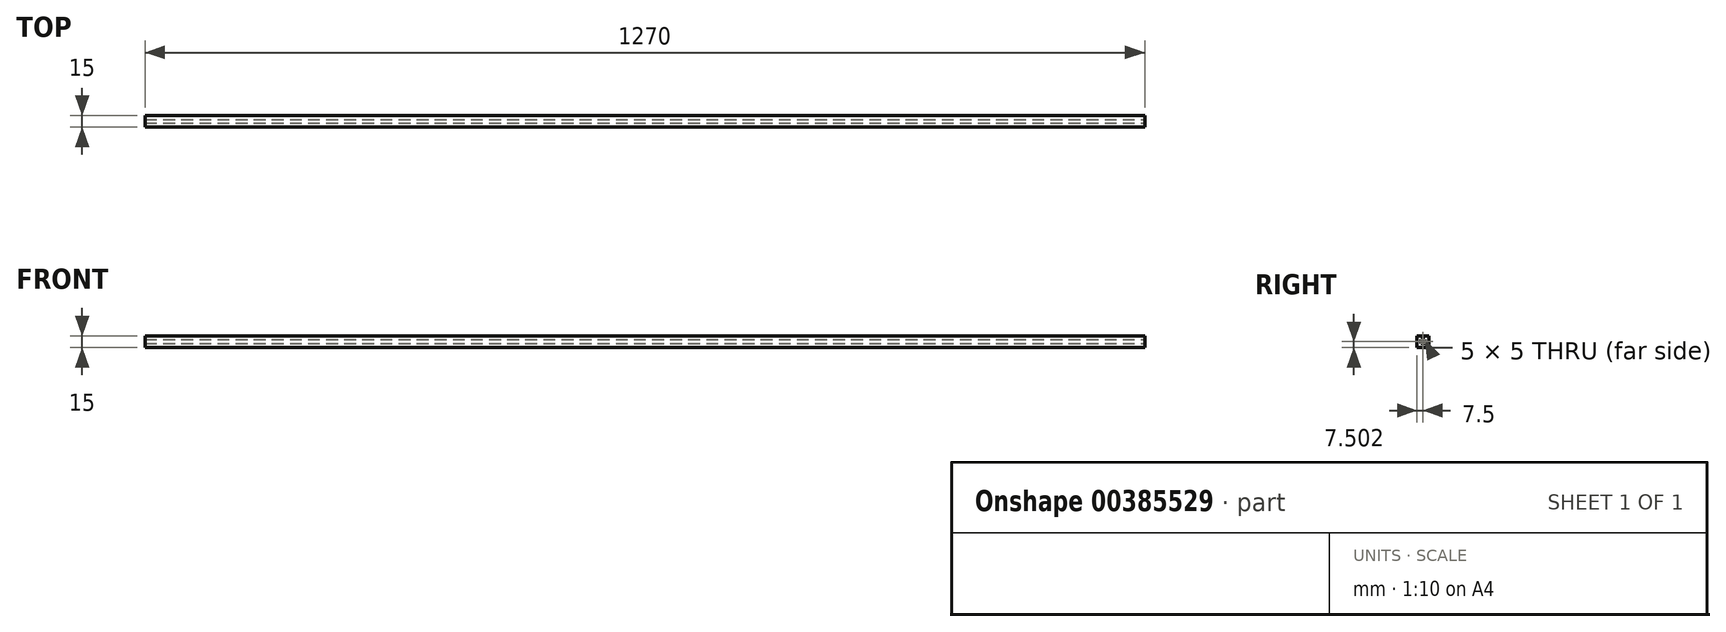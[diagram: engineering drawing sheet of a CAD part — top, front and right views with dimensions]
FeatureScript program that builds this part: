
annotation { "Feature Type Name" : "Feature", "Feature Type Description" : "" }
export const myFeature = defineFeature(function(context is Context, id is Id, definition is map)
    precondition{}
    {
        {
            var Q0;
            Q0=qCreatedBy(makeId("Front.planeOp"),FACE);
            var sketch = newSketch(context, id + "F0", { "sketchPlane" : qUnion([Q0])});
            skLineSegment(sketch, "E0.bottom", {"start": v(-638.32, -20.5) * mm, "end": v(631.68, -20.5) * mm});
            skLineSegment(sketch, "E0.top", {"start": v(-638.32, -35.5) * mm, "end": v(631.68, -35.5) * mm});
            skLineSegment(sketch, "E0.left", {"start": v(-638.32, -20.5) * mm, "end": v(-638.32, -35.5) * mm});
            skLineSegment(sketch, "E0.right", {"start": v(631.68, -20.5) * mm, "end": v(631.68, -35.5) * mm});
            skSolve(sketch);
        }
        {
            var Q0;
            Q0=makeQuery(id+"F0.imprint","IMPRINT",FACE,{"disambiguationData":[TD([[makeQuery(id+"F0.imprint","IMPRINT",EDGE,{"derivedFrom":sQuery(id+"F0.wireOp",EDGE,"E0.bottom")}),-1.0]])]});
            extrude(context, id + "F1", {"entities" : qUnion([Q0]), "endBound" : BoundingType.SYMMETRIC, "depth" : 15 * mm});
        }
        {
            var Q0;
            Q0=makeQuery(id+"F1.opExtrude","SWEPT_FACE",FACE,{"disambiguationData":[OSD([sQuery(id+"F0.wireOp",EDGE,"E0.right")])]});
            var sketch = newSketch(context, id + "F2", { "sketchPlane" : qUnion([Q0])});
            skLineSegment(sketch, "E1.0", {"start": v(2.5, -30.5) * mm, "end": v(2.5, -25.5) * mm});
            skLineSegment(sketch, "E1.1", {"start": v(-2.5, -30.5) * mm, "end": v(2.5, -30.5) * mm});
            skLineSegment(sketch, "E1.2", {"start": v(-2.5, -25.5) * mm, "end": v(-2.5, -30.5) * mm});
            skLineSegment(sketch, "E1.3", {"start": v(2.5, -25.5) * mm, "end": v(-2.5, -25.5) * mm});
            skSolve(sketch);
        }
        {
            var Q0;
            Q0=makeQuery(id+"F2.imprint","IMPRINT",FACE,{"disambiguationData":[TD([[makeQuery(id+"F2.imprint","IMPRINT",EDGE,{"derivedFrom":sQuery(id+"F2.wireOp",EDGE,"E1.0")}),1.0]])]});
            extrude(context, id + "F3", {"entities" : qUnion([Q0]), "operationType" : NewBodyOperationType.REMOVE, "endBound" : BoundingType.SYMMETRIC, "oppositeDirection" : true, "depth" : 381 * mm});
        }
        {
            var Q0;
            Q0=makeQuery(id+"F3.boolean.opBoolean","COPY",FACE,{"derivedFrom":makeQuery(id+"F3.opExtrude","CAP_FACE",FACE,{"disambiguationData":[OSD([sQuery(id+"F2.wireOp",EDGE,"E1.0"),sQuery(id+"F2.wireOp",EDGE,"E1.1"),sQuery(id+"F2.wireOp",EDGE,"E1.2"),sQuery(id+"F2.wireOp",EDGE,"E1.3")])],"isStart":false})});
            extrude(context, id + "F4", {"entities" : qUnion([Q0]), "operationType" : NewBodyOperationType.REMOVE, "oppositeDirection" : true, "depth" : 1270 * mm});
        }
    });
